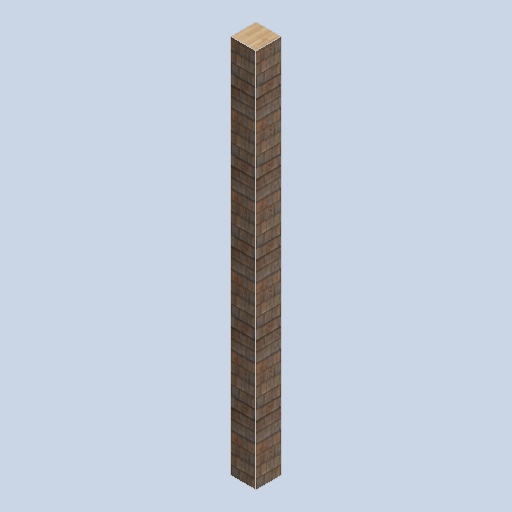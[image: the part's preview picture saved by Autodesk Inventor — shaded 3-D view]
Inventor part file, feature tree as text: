
AUTODESK INVENTOR PART (.ipt)
format: ipt  version: 2024.2 (Build 282272000, 272)  size: 315,904 bytes
history: native  units: mm
features: extrude x1, sketch x1
ambient origin geometry x8: Origin, YZ Plane, XZ Plane, XY Plane, X Axis, Y Axis, Z Axis, Center Point
bodies: Solid1 (feature_tree)
feature tree (2):
  extrude  "Extrusion1"  Depth=400.0mm
  sketch  "Sketch1"  dims[d0=400.0mm d1=400.0mm d2=6073.0mm d3=0.0mm]
